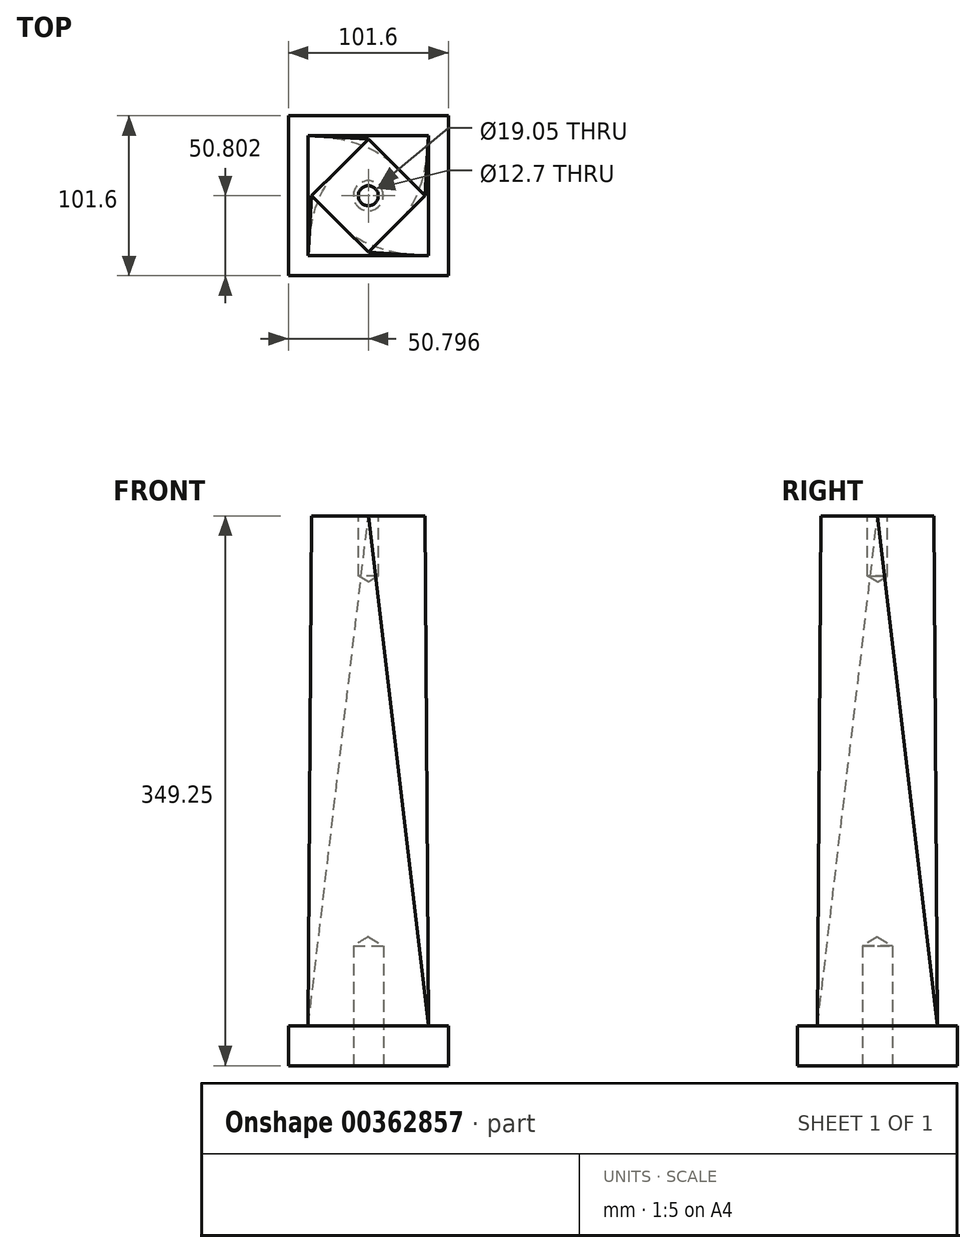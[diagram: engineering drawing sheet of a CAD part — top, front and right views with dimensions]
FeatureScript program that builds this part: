
annotation { "Feature Type Name" : "Feature", "Feature Type Description" : "" }
export const myFeature = defineFeature(function(context is Context, id is Id, definition is map)
    precondition{}
    {
        {
            var Q0;
            Q0=qCreatedBy(makeId("Top.planeOp"),FACE);
            var sketch = newSketch(context, id + "F0", { "sketchPlane" : qUnion([Q0])});
            skLineSegment(sketch, "E0.bottom", {"start": v(-52.11, 76.72) * mm, "end": v(49.49, 76.72) * mm});
            skLineSegment(sketch, "E0.top", {"start": v(-52.11, -24.88) * mm, "end": v(49.49, -24.88) * mm});
            skLineSegment(sketch, "E0.left", {"start": v(-52.11, 76.72) * mm, "end": v(-52.11, -24.88) * mm});
            skLineSegment(sketch, "E0.right", {"start": v(49.49, 76.72) * mm, "end": v(49.49, -24.88) * mm});
            skLineSegment(sketch, "E1.0", {"start": v(-39.41, 64.02) * mm, "end": v(36.79, 64.02) * mm});
            skLineSegment(sketch, "E1.1", {"start": v(-39.41, 64.02) * mm, "end": v(-39.41, -12.18) * mm});
            skLineSegment(sketch, "E1.2", {"start": v(-39.41, -12.18) * mm, "end": v(36.79, -12.18) * mm});
            skLineSegment(sketch, "E1.3", {"start": v(36.79, 64.02) * mm, "end": v(36.79, -12.18) * mm});
            skPoint(sketch, "E2", {"position": v(-1.31, 25.92) * mm});
            skPoint(sketch, "E2.positionSnap0", {"position": v(-1.31, 64.02) * mm});
            skPoint(sketch, "E2.positionSnap1", {"position": v(-39.41, 25.92) * mm});
            skSolve(sketch);
        }
        {
            var Q0;
            Q0 = qSketchRegion(id + "F0", true);
            var Q1;
            Q1=makeQuery(id+"F0.imprint","IMPRINT",FACE,{"disambiguationData":[TD([[makeQuery(id+"F0.imprint","IMPRINT",EDGE,{"derivedFrom":sQuery(id+"F0.wireOp",EDGE,"E1.0")}),-1.0]])]});
            extrude(context, id + "F1", {"entities" : qUnion([Q0, Q1]), "depth" : 25.4 * mm});
        }
        {
            var Q0;
            Q0=makeQuery(id+"F1.opExtrude","CAP_FACE",FACE,{"disambiguationData":[OSD([sQuery(id+"F0.wireOp",EDGE,"E0.bottom"),sQuery(id+"F0.wireOp",EDGE,"E0.top"),sQuery(id+"F0.wireOp",EDGE,"E0.left"),sQuery(id+"F0.wireOp",EDGE,"E0.right")])],"isStart":false});
            var sketch = newSketch(context, id + "F2", { "sketchPlane" : qUnion([Q0])});
            skLineSegment(sketch, "E3.0", {"start": v(-39.41, 64.02) * mm, "end": v(36.79, 64.02) * mm});
            skLineSegment(sketch, "E4.0", {"start": v(36.79, 64.02) * mm, "end": v(36.79, -12.18) * mm});
            skLineSegment(sketch, "E5.0", {"start": v(-39.41, -12.18) * mm, "end": v(36.79, -12.18) * mm});
            skLineSegment(sketch, "E6.0", {"start": v(-39.41, 64.02) * mm, "end": v(-39.41, -12.18) * mm});
            skSolve(sketch);
        }
        {
            var Q0;
            Q0=qCreatedBy(makeId("Top.planeOp"),FACE);
            cPlane(context, id + "F3", {"entities" : qUnion([Q0]), "cplaneType" : CPlaneType.OFFSET, "offset" : 349.25 * mm, "width" : 152.4 * mm, "height" : 152.4 * mm});
        }
        {
            var Q0;
            Q0=qCreatedBy(id+"F3.planeOp",FACE);
            var sketch = newSketch(context, id + "F4", { "sketchPlane" : qUnion([Q0])});
            skPoint(sketch, "E7.0", {"position": v(139.66, -12.18) * mm});
            skLineSegment(sketch, "E8.0", {"start": v(34.6, 25.92) * mm, "end": v(-1.31, 61.84) * mm});
            skLineSegment(sketch, "E8.1", {"start": v(-1.31, -10) * mm, "end": v(34.6, 25.92) * mm});
            skLineSegment(sketch, "E8.2", {"start": v(-37.24, 25.92) * mm, "end": v(-1.31, -10) * mm});
            skLineSegment(sketch, "E8.3", {"start": v(-1.31, 61.84) * mm, "end": v(-37.24, 25.92) * mm});
            skPoint(sketch, "E9", {"position": v(-1.31, 25.92) * mm});
            skSolve(sketch);
        }
        {
            var Q1;
            Q1=makeQuery(id+"F2.imprint","IMPRINT",FACE,{"disambiguationData":[TD([[makeQuery(id+"F2.imprint","IMPRINT",EDGE,{"derivedFrom":sQuery(id+"F2.wireOp",EDGE,"E3.0")}),-1.0]])]});
            var Q2;
            Q2=makeQuery(id+"F4.imprint","IMPRINT",FACE,{"disambiguationData":[TD([[makeQuery(id+"F4.imprint","IMPRINT",EDGE,{"derivedFrom":sQuery(id+"F4.wireOp",EDGE,"E8.0")}),1.0]])]});
            var Q3;
            Q3=sQuery(id+"F4.wireOp",VERTEX,"E8.2.end");
            var Q4;
            Q4=sQuery(id+"F2.wireOp",VERTEX,"E5.0.end");
            loft(context, id + "F5", {"operationType" : NewBodyOperationType.ADD, "sheetProfilesArray" : [{ "sheetProfileEntities" : qUnion([Q1]) }, { "sheetProfileEntities" : qUnion([Q2]) }], "matchConnections" : true, "connections" : [{ "connectionEntities" : qUnion([Q3, Q4]), "connectionEdgeQueries" : qUnion([]), "connectionEdgeParameters" : [] }]});
        }
        {
            var Q0;
            Q0=sQuery(id+"F0.wireOp",VERTEX,"E2");
            var Q1;
            Q1=makeQuery(id+"F1.opExtrude","SWEPT_BODY",BODY,{"disambiguationData":[OSD([sQuery(id+"F0.wireOp",EDGE,"E0.bottom"),sQuery(id+"F0.wireOp",EDGE,"E0.top"),sQuery(id+"F0.wireOp",EDGE,"E0.left"),sQuery(id+"F0.wireOp",EDGE,"E0.right")])]});
            hole(context, id + "F6", {"style" : HoleStyle.SIMPLE, "endStyle" : HoleEndStyle.BLIND, "oppositeDirection" : true, "holeDiameter" : 19.05 * mm, "holeDepth" : 76.2 * mm, "tappedDepth" : 12.7 * mm, "tapClearance" : 3, "startFromSketch" : true, "locations" : qUnion([Q0]), "scope" : qUnion([Q1])});
        }
        {
            var Q0;
            Q0=sQuery(id+"F4.wireOp",VERTEX,"E9");
            var Q1;
            Q1=makeQuery(id+"F1.opExtrude","SWEPT_BODY",BODY,{"disambiguationData":[OSD([sQuery(id+"F0.wireOp",EDGE,"E0.bottom"),sQuery(id+"F0.wireOp",EDGE,"E0.top"),sQuery(id+"F0.wireOp",EDGE,"E0.left"),sQuery(id+"F0.wireOp",EDGE,"E0.right")])]});
            hole(context, id + "F7", {"style" : HoleStyle.SIMPLE, "endStyle" : HoleEndStyle.BLIND, "holeDiameter" : 12.7 * mm, "holeDepth" : 38.1 * mm, "tappedDepth" : 12.7 * mm, "tapClearance" : 3, "startFromSketch" : true, "locations" : qUnion([Q0]), "scope" : qUnion([Q1])});
        }
    });
